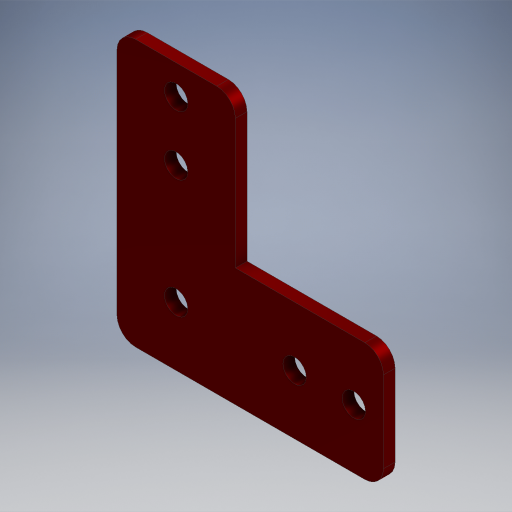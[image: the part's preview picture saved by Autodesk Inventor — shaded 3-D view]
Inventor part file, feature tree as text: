
AUTODESK INVENTOR PART (.ipt)
format: ipt  version: 2024.2 (Build 282272000, 272)  size: 325,632 bytes
history: native  units: in
note: dims shown in document units (in); Inventor stores cm internally (conversion verified against a paired STEP export)
features: extrude x1, fillet x1, sketch x1, projected_geometry x1, other x1
ambient origin geometry x8: Origin, YZ Plane, XZ Plane, XY Plane, X Axis, Y Axis, Z Axis, Center Point
bodies: Solid1 (feature_tree)
feature tree (5):
  extrude  "Extrusion1"  Depth=0.157in
  fillet  "Fillet1"  Radius=1.0in
  sketch  "Sketch1"  dims[d0=0.5in d1=0.5in d2=1.0in d3=0.0in d4=0.157in]
  projected_geometry  "Projected Loop1"
  other  "TTB-0082 - Aluminum L Gusset - 5mm Hole Size"
